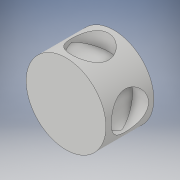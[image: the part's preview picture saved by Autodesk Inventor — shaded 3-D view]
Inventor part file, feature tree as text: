
AUTODESK INVENTOR PART (.ipt)
format: ipt  version: 2019 (Build 230136000, 136)  size: 192,512 bytes
history: native  units: mm
features: sketch x5, extrude x5, pattern_circular x1, fillet x1
ambient origin geometry x8: Origin, YZ Plane, XZ Plane, XY Plane, X Axis, Y Axis, Z Axis, Center Point
bodies: Solide1 (feature_tree)
feature tree (12):
  sketch  "Esquisse1"
  extrude  "Extrusion1"  Depth=30.0mm
  sketch  "Esquisse3"
  extrude  "Extrusion2"  Depth=3.0mm
  extrude  "Extrusion3"  Depth=7.0mm
  extrude  "Extrusion4"  Depth=3.0mm
  pattern_circular  "Réseau circulaire1"  Count=3  [1 undecoded]
  extrude  "Extrusion5"  Depth=18.0mm TaperAngle=0.0deg
  fillet  "Congé1"  Radius=14.0mm
  sketch  "Esquisse2"
  sketch  "Esquisse4"
  sketch  "Esquisse5"
note: 1 required parameter value undecoded (feature->parameter linkage not recoverable at this tier; creation-order binding heuristic only, values carry confidence <= 0.55)
